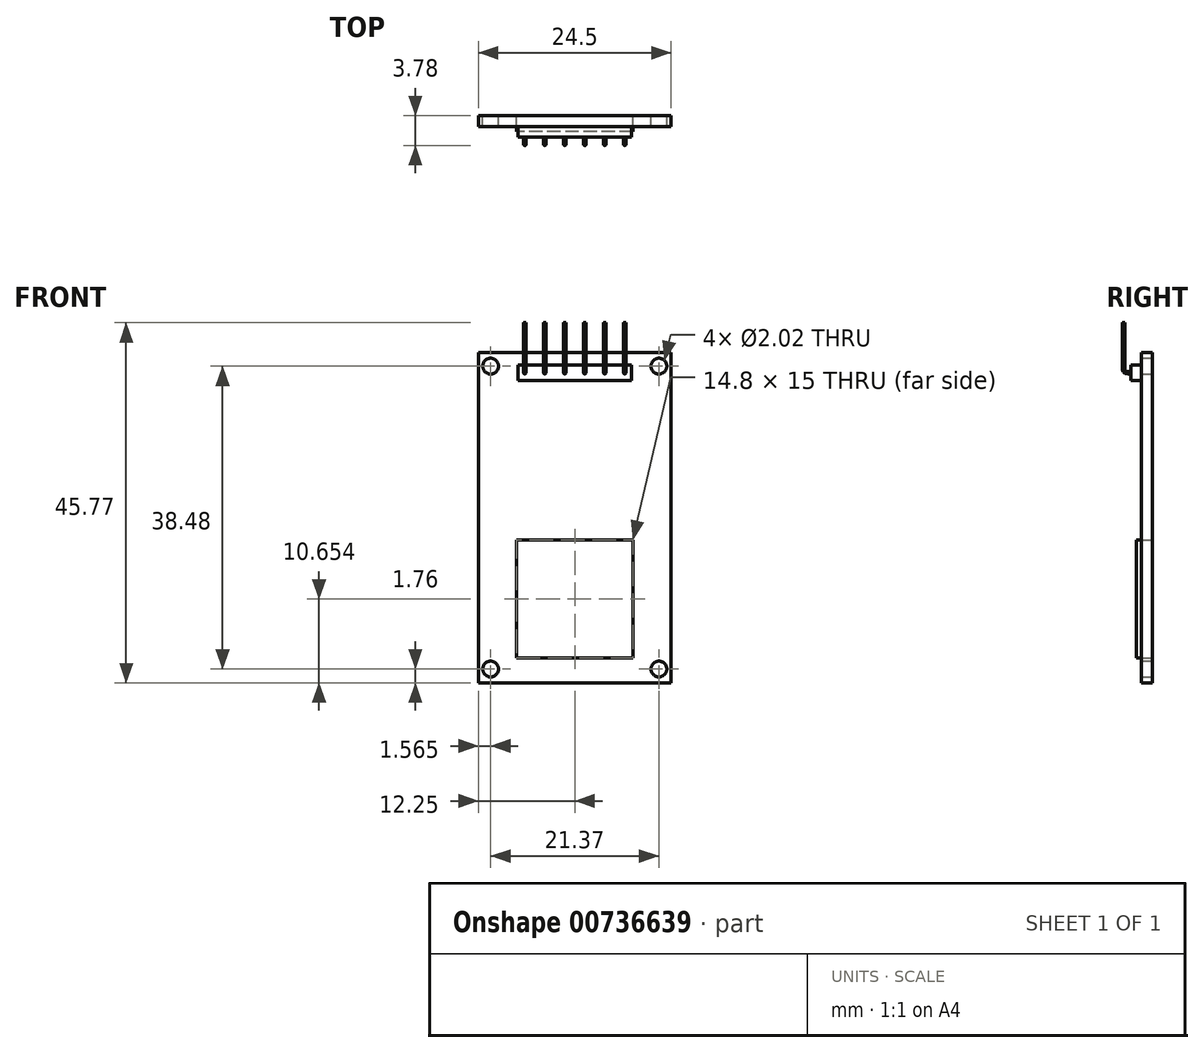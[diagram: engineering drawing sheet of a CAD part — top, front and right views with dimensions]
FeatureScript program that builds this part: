
annotation { "Feature Type Name" : "Feature", "Feature Type Description" : "" }
export const myFeature = defineFeature(function(context is Context, id is Id, definition is map)
    precondition{}
    {
        {
            var Q0;
            Q0=qCreatedBy(makeId("Front.planeOp"),FACE);
            var sketch = newSketch(context, id + "F0", { "sketchPlane" : qUnion([Q0])});
            skLineSegment(sketch, "E0.bottom", {"start": v(12.25, 21) * mm, "end": v(-12.25, 21) * mm});
            skLineSegment(sketch, "E0.top", {"start": v(12.25, -21) * mm, "end": v(-12.25, -21) * mm});
            skLineSegment(sketch, "E0.left", {"start": v(12.25, 21) * mm, "end": v(12.25, -21) * mm});
            skLineSegment(sketch, "E0.right", {"start": v(-12.25, 21) * mm, "end": v(-12.25, -21) * mm});
            skPoint(sketch, "E0.middle", {"position": v(0, 0) * mm});
            skCircle(sketch, "E1", {"center": v(-10.69, 19.24) * mm, "radius": 1 * mm});
            skCircle(sketch, "E2.MirrorC", {"center": v(10.69, 19.24) * mm, "radius": 1 * mm});
            skCircle(sketch, "E3.MirrorC", {"center": v(-10.69, -19.24) * mm, "radius": 1 * mm});
            skCircle(sketch, "E4.MirrorC", {"center": v(10.69, -19.24) * mm, "radius": 1 * mm});
            skLineSegment(sketch, "E5.bottom", {"start": v(7.4, -2.85) * mm, "end": v(-7.4, -2.85) * mm});
            skLineSegment(sketch, "E5.top", {"start": v(7.4, -17.85) * mm, "end": v(-7.4, -17.85) * mm});
            skLineSegment(sketch, "E5.left", {"start": v(7.4, -2.85) * mm, "end": v(7.4, -17.85) * mm});
            skLineSegment(sketch, "E5.right", {"start": v(-7.4, -2.85) * mm, "end": v(-7.4, -17.85) * mm});
            skPoint(sketch, "E5.middle", {"position": v(0, -10.35) * mm});
            skLineSegment(sketch, "E6.bottom", {"start": v(7.2, 19.41) * mm, "end": v(-7.2, 19.41) * mm});
            skLineSegment(sketch, "E6.top", {"start": v(7.2, 17.41) * mm, "end": v(-7.2, 17.41) * mm});
            skLineSegment(sketch, "E6.left", {"start": v(7.2, 19.41) * mm, "end": v(7.2, 17.41) * mm});
            skLineSegment(sketch, "E6.right", {"start": v(-7.2, 19.41) * mm, "end": v(-7.2, 17.41) * mm});
            skPoint(sketch, "E6.middle", {"position": v(0, 18.41) * mm});
            skCircle(sketch, "E7", {"center": v(-6.35, 18.41) * mm, "radius": 0.15 * mm});
            skCircle(sketch, "E8.1.0.0", {"center": v(-3.81, 18.41) * mm, "radius": 0.15 * mm});
            skCircle(sketch, "E8.2.0.0", {"center": v(-1.27, 18.41) * mm, "radius": 0.15 * mm});
            skCircle(sketch, "E8.3.0.0", {"center": v(1.27, 18.41) * mm, "radius": 0.15 * mm});
            skCircle(sketch, "E8.4.0.0", {"center": v(3.8, 18.41) * mm, "radius": 0.15 * mm});
            skCircle(sketch, "E8.5.0.0", {"center": v(6.35, 18.41) * mm, "radius": 0.15 * mm});
            skLineSegment(sketch, "E8.direction1", {"start": v(-6.35, 18.41) * mm, "end": v(-3.81, 18.41) * mm, "construction": true});
            skSolve(sketch);
        }
        {
            var Q0;
            Q0=makeQuery(id+"F0.imprint","IMPRINT",FACE,{"disambiguationData":[TD([[makeQuery(id+"F0.imprint","IMPRINT",EDGE,{"derivedFrom":sQuery(id+"F0.wireOp",EDGE,"E0.bottom")}),1.0]])]});
            extrude(context, id + "F1", {"entities" : qUnion([Q0]), "depth" : 1.35 * mm, "offsetDistance" : 25 * mm});
        }
        {
            var Q0;
            Q0=makeQuery(id+"F0.imprint","IMPRINT",FACE,{"disambiguationData":[TD([[makeQuery(id+"F0.imprint","IMPRINT",EDGE,{"derivedFrom":sQuery(id+"F0.wireOp",EDGE,"E5.bottom")}),1.0]])]});
            extrude(context, id + "F2", {"entities" : qUnion([Q0]), "depth" : 2 * mm, "offsetDistance" : 25 * mm});
        }
        {
            var Q0;
            Q0=qCreatedBy(makeId("Right.planeOp"),FACE);
            var sketch = newSketch(context, id + "F3", { "sketchPlane" : qUnion([Q0])});
            skPoint(sketch, "E9", {"position": v(0, 18.41) * mm});
            skLineSegment(sketch, "E10", {"start": v(0, 18.41) * mm, "end": v(-2.8, 18.41) * mm});
            skLineSegment(sketch, "E11", {"start": v(-3.63, 18.77) * mm, "end": v(-3.63, 24.77) * mm});
            skFitSpline(sketch, "E12", {"points": [v(-2.8, 18.41) * mm, v(-3.4, 18.48) * mm, v(-3.63, 18.77) * mm], "startDerivative": vector(-1.7, 0.07) * mm, "endDerivative": vector(-0.18, 1.32) * mm});
            skSolve(sketch);
        }
        {
            var Q0;
            Q0=makeQuery(id+"F0.imprint","IMPRINT",FACE,{"disambiguationData":[TD([[makeQuery(id+"F0.imprint","IMPRINT",EDGE,{"derivedFrom":sQuery(id+"F0.wireOp",EDGE,"E6.bottom")}),1.0]])]});
            extrude(context, id + "F4", {"entities" : qUnion([Q0]), "operationType" : NewBodyOperationType.ADD, "depth" : 2.7 * mm, "offsetDistance" : 25 * mm});
        }
        {
            var Q0;
            Q0=makeQuery(id+"F0.imprint","IMPRINT",FACE,{"disambiguationData":[TD([[makeQuery(id+"F0.imprint","IMPRINT",EDGE,{"derivedFrom":sQuery(id+"F0.wireOp",EDGE,"E7")}),1.0]])]});
            var Q1;
            Q1=makeQuery(id+"F0.imprint","IMPRINT",FACE,{"disambiguationData":[TD([[makeQuery(id+"F0.imprint","IMPRINT",EDGE,{"derivedFrom":sQuery(id+"F0.wireOp",EDGE,"E8.1.0.0")}),1.0]])]});
            var Q2;
            Q2=makeQuery(id+"F0.imprint","IMPRINT",FACE,{"disambiguationData":[TD([[makeQuery(id+"F0.imprint","IMPRINT",EDGE,{"derivedFrom":sQuery(id+"F0.wireOp",EDGE,"E8.2.0.0")}),1.0]])]});
            var Q3;
            Q3=makeQuery(id+"F0.imprint","IMPRINT",FACE,{"disambiguationData":[TD([[makeQuery(id+"F0.imprint","IMPRINT",EDGE,{"derivedFrom":sQuery(id+"F0.wireOp",EDGE,"E8.3.0.0")}),1.0]])]});
            var Q4;
            Q4=makeQuery(id+"F0.imprint","IMPRINT",FACE,{"disambiguationData":[TD([[makeQuery(id+"F0.imprint","IMPRINT",EDGE,{"derivedFrom":sQuery(id+"F0.wireOp",EDGE,"E8.4.0.0")}),1.0]])]});
            var Q5;
            Q5=makeQuery(id+"F0.imprint","IMPRINT",FACE,{"disambiguationData":[TD([[makeQuery(id+"F0.imprint","IMPRINT",EDGE,{"derivedFrom":sQuery(id+"F0.wireOp",EDGE,"E8.5.0.0")}),1.0]])]});
            var Q6;
            Q6=sQuery(id+"F3.wireOp",EDGE,"E12");
            var Q7;
            Q7=sQuery(id+"F3.wireOp",EDGE,"E11");
            var Q8;
            Q8=sQuery(id+"F3.wireOp",EDGE,"E10");
            sweep(context, id + "F5", {"operationType" : NewBodyOperationType.ADD, "profiles" : qUnion([Q0, Q1, Q2, Q3, Q4, Q5]), "path" : qUnion([Q6, Q7, Q8])});
        }
    });
